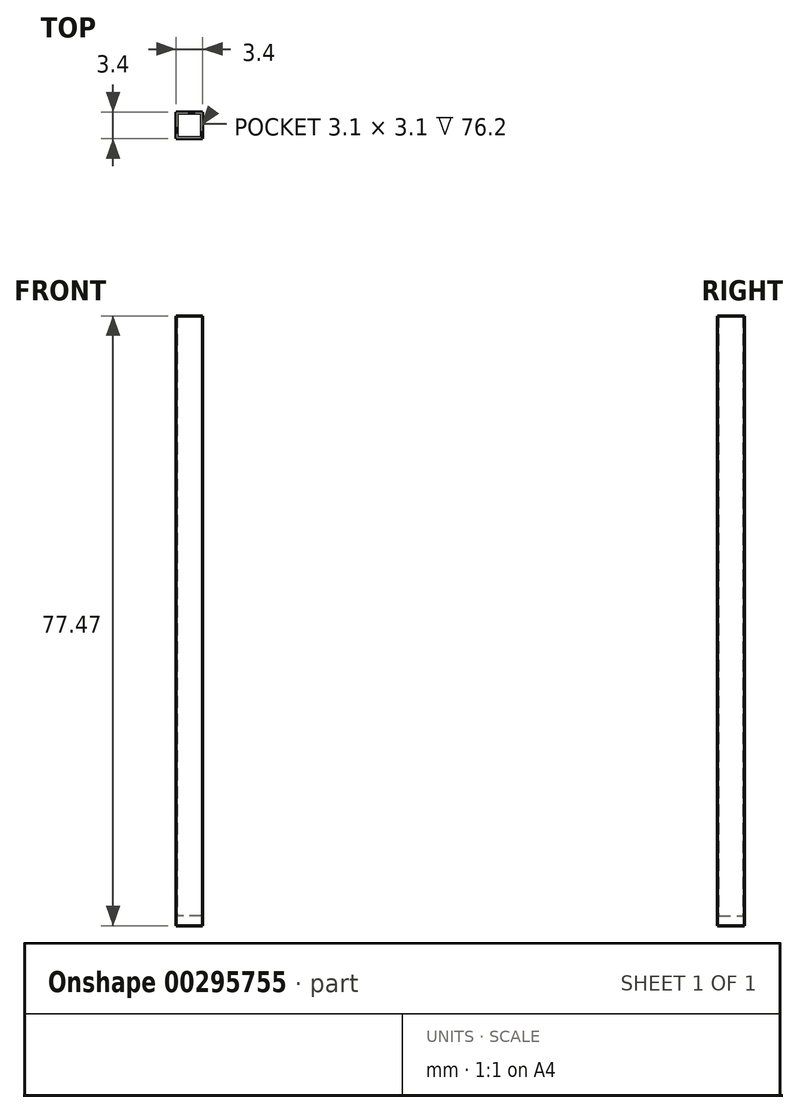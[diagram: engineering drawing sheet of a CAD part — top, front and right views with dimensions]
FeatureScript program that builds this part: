
annotation { "Feature Type Name" : "Feature", "Feature Type Description" : "" }
export const myFeature = defineFeature(function(context is Context, id is Id, definition is map)
    precondition{}
    {
        {
            var Q0;
            Q0=qCreatedBy(makeId("Top.planeOp"),FACE);
            var sketch = newSketch(context, id + "F0", { "sketchPlane" : qUnion([Q0])});
            skLineSegment(sketch, "E0.bottom", {"start": v(1.55, -1.55) * mm, "end": v(-1.55, -1.55) * mm});
            skLineSegment(sketch, "E0.top", {"start": v(1.55, 1.55) * mm, "end": v(-1.55, 1.55) * mm});
            skLineSegment(sketch, "E0.left", {"start": v(1.55, -1.55) * mm, "end": v(1.55, 1.55) * mm});
            skLineSegment(sketch, "E0.right", {"start": v(-1.55, -1.55) * mm, "end": v(-1.55, 1.55) * mm});
            skPoint(sketch, "E0.middle", {"position": v(0, 0) * mm});
            skLineSegment(sketch, "E1.bottom", {"start": v(1.7, -1.7) * mm, "end": v(-1.7, -1.7) * mm});
            skLineSegment(sketch, "E1.top", {"start": v(1.7, 1.7) * mm, "end": v(-1.7, 1.7) * mm});
            skLineSegment(sketch, "E1.left", {"start": v(1.7, -1.7) * mm, "end": v(1.7, 1.7) * mm});
            skLineSegment(sketch, "E1.right", {"start": v(-1.7, -1.7) * mm, "end": v(-1.7, 1.7) * mm});
            skSolve(sketch);
        }
        {
            var Q0;
            Q0 = qSketchRegion(id + "F0", true);
            var Q1;
            Q1=makeQuery(id+"F0.imprint","IMPRINT",FACE,{"disambiguationData":[TD([[makeQuery(id+"F0.imprint","IMPRINT",EDGE,{"derivedFrom":sQuery(id+"F0.wireOp",EDGE,"E0.bottom")}),-1.0]])]});
            extrude(context, id + "F1", {"entities" : qUnion([Q0, Q1]), "oppositeDirection" : true, "depth" : 1.27 * mm});
        }
        {
            var Q0;
            Q0=makeQuery(id+"F0.imprint","IMPRINT",FACE,{"disambiguationData":[TD([[makeQuery(id+"F0.imprint","IMPRINT",EDGE,{"derivedFrom":sQuery(id+"F0.wireOp",EDGE,"E0.bottom")}),1.0]])]});
            extrude(context, id + "F2", {"entities" : qUnion([Q0]), "operationType" : NewBodyOperationType.ADD, "depth" : 76.2 * mm});
        }
    });
